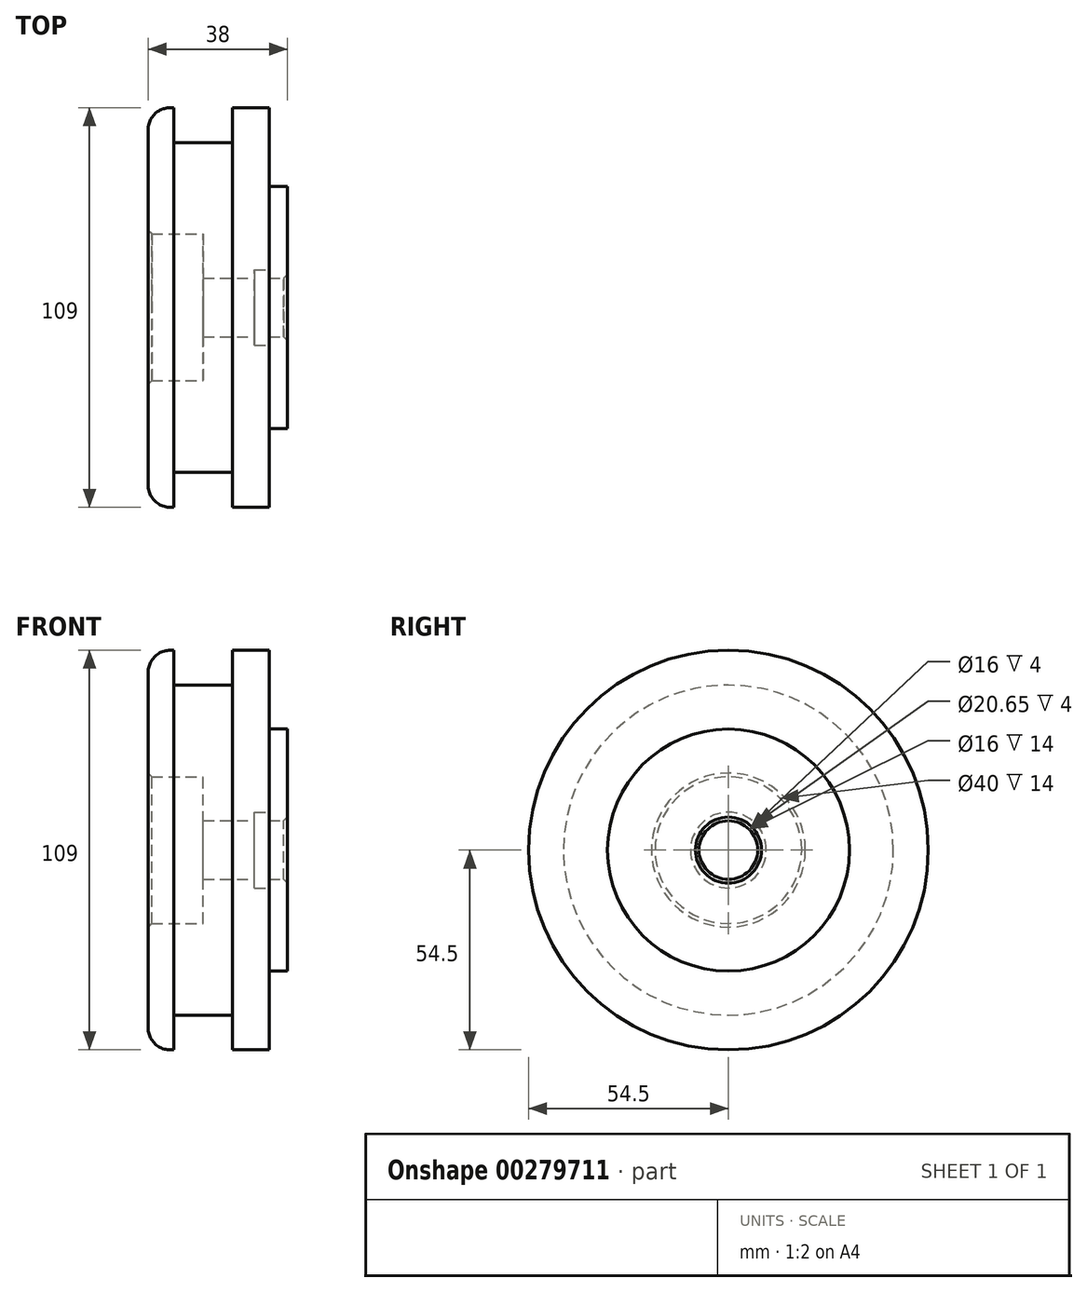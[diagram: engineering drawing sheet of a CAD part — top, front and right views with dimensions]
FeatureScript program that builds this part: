
annotation { "Feature Type Name" : "Feature", "Feature Type Description" : "" }
export const myFeature = defineFeature(function(context is Context, id is Id, definition is map)
    precondition{}
    {
        {
            var Q0;
            Q0=qCreatedBy(makeId("Front.planeOp"),FACE);
            var sketch = newSketch(context, id + "F0", { "sketchPlane" : qUnion([Q0])});
            skLineSegment(sketch, "E0", {"start": v(43.31, 0) * mm, "end": v(-50.24, 0) * mm, "construction": true});
            skLineSegment(sketch, "E1", {"start": v(-30.78, -20) * mm, "end": v(-15.78, -20) * mm});
            skLineSegment(sketch, "E2", {"start": v(-15.78, -20) * mm, "end": v(-15.78, -8) * mm});
            skLineSegment(sketch, "E3", {"start": v(-30.78, -20) * mm, "end": v(-30.78, -54.5) * mm});
            skLineSegment(sketch, "E4", {"start": v(-30.78, -54.5) * mm, "end": v(-23.78, -54.5) * mm});
            skLineSegment(sketch, "E5", {"start": v(-15.78, -8) * mm, "end": v(-1.78, -8) * mm});
            skPoint(sketch, "E6.orphan", {"position": v(-30.78, 0) * mm});
            skLineSegment(sketch, "E7", {"start": v(7.22, -8) * mm, "end": v(7.22, -33) * mm});
            skPoint(sketch, "E8.orphan", {"position": v(7.22, 0) * mm});
            skLineSegment(sketch, "E9", {"start": v(7.22, -33) * mm, "end": v(2.22, -33) * mm});
            skLineSegment(sketch, "E10", {"start": v(2.22, -33) * mm, "end": v(2.22, -54.5) * mm});
            skLineSegment(sketch, "E11", {"start": v(-7.78, -54.5) * mm, "end": v(-7.78, -45) * mm});
            skLineSegment(sketch, "E12", {"start": v(-7.78, -45) * mm, "end": v(-23.78, -45) * mm});
            skLineSegment(sketch, "E13", {"start": v(-23.78, -45) * mm, "end": v(-23.78, -54.5) * mm});
            skLineSegment(sketch, "E14.trimOffspring", {"start": v(-7.78, -54.5) * mm, "end": v(2.22, -54.5) * mm});
            skLineSegment(sketch, "E15", {"start": v(2.22, -8) * mm, "end": v(2.22, -10.33) * mm});
            skLineSegment(sketch, "E16", {"start": v(2.22, -10.33) * mm, "end": v(-1.78, -10.33) * mm});
            skLineSegment(sketch, "E17", {"start": v(-1.78, -10.33) * mm, "end": v(-1.78, -8) * mm});
            skLineSegment(sketch, "E18.trimOffspring", {"start": v(2.22, -8) * mm, "end": v(7.22, -8) * mm});
            skSolve(sketch);
        }
        {
            var Q0;
            Q0=makeQuery(id+"F0.imprint","IMPRINT",FACE,{"disambiguationData":[TD([[makeQuery(id+"F0.imprint","IMPRINT",EDGE,{"derivedFrom":sQuery(id+"F0.wireOp",EDGE,"E1")}),-1.0]])]});
            var Q1;
            Q1=sQuery(id+"F0.wireOp",EDGE,"E0");
            revolve(context, id + "F1", {"entities" : qUnion([Q0]), "axis" : qUnion([Q1]), "revolveType" : RevolveType.FULL});
        }
        {
            var Q0;
            Q0=makeQuery(id+"F1.opRevolve","SWEPT_EDGE",EDGE,{"disambiguationData":[OSD([sQuery(id+"F0.wireOp",EDGE,"E3"),sQuery(id+"F0.wireOp",EDGE,"E4")])]});
            fillet(context, id + "F2", {"entities" : qUnion([Q0]), "radius" : 6 * mm, "tangentPropagation" : true, "allowEdgeOverflow" : false});
        }
        {
            var Q0;
            Q0=makeQuery(id+"F1.opRevolve","SWEPT_EDGE",EDGE,{"disambiguationData":[OSD([sQuery(id+"F0.wireOp",EDGE,"E1"),sQuery(id+"F0.wireOp",EDGE,"E3")])]});
            var Q1;
            Q1=makeQuery(id+"F1.opRevolve","SWEPT_EDGE",EDGE,{"disambiguationData":[OSD([sQuery(id+"F0.wireOp",EDGE,"E7"),sQuery(id+"F0.wireOp",EDGE,"E18.trimOffspring")])]});
            chamfer(context, id + "F3", {"entities" : qUnion([Q0, Q1]), "width" : 1 * mm, "tangentPropagation" : true});
        }
    });
